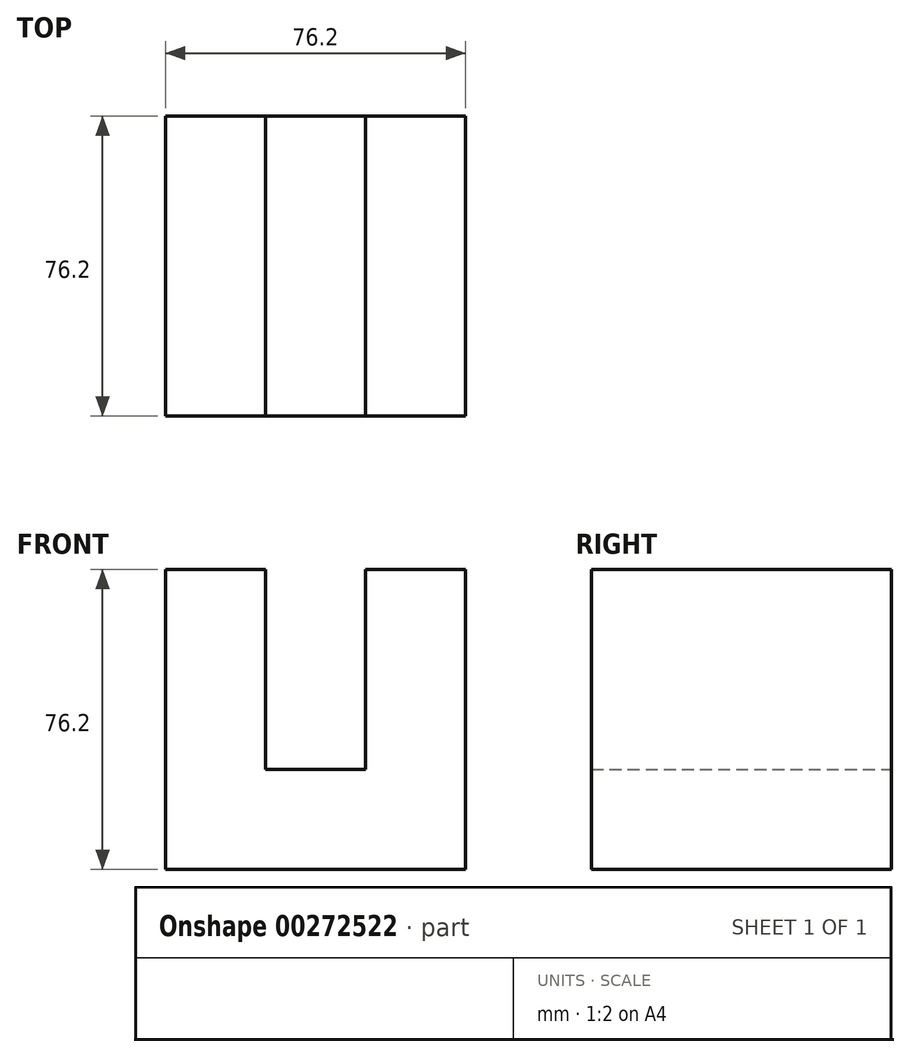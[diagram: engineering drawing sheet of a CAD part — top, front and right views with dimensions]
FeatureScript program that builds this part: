
annotation { "Feature Type Name" : "Feature", "Feature Type Description" : "" }
export const myFeature = defineFeature(function(context is Context, id is Id, definition is map)
    precondition{}
    {
        {
            var Q0;
            Q0=qCreatedBy(makeId("Front.planeOp"),FACE);
            var sketch = newSketch(context, id + "F0", { "sketchPlane" : qUnion([Q0])});
            skLineSegment(sketch, "E0", {"start": v(0, 0) * mm, "end": v(-76.2, 0) * mm});
            skLineSegment(sketch, "E1", {"start": v(-76.2, 0) * mm, "end": v(-76.2, 76.2) * mm});
            skLineSegment(sketch, "E2", {"start": v(-76.2, 76.2) * mm, "end": v(-50.8, 76.2) * mm});
            skLineSegment(sketch, "E3", {"start": v(-50.8, 76.2) * mm, "end": v(-50.8, 25.4) * mm});
            skLineSegment(sketch, "E4", {"start": v(-50.8, 25.4) * mm, "end": v(-25.4, 25.4) * mm});
            skLineSegment(sketch, "E5", {"start": v(-25.4, 25.4) * mm, "end": v(-25.4, 76.2) * mm});
            skLineSegment(sketch, "E6", {"start": v(-25.4, 76.2) * mm, "end": v(0, 76.2) * mm});
            skLineSegment(sketch, "E7", {"start": v(0, 76.2) * mm, "end": v(0, 0) * mm});
            skSolve(sketch);
        }
        {
            var Q0;
            Q0 = qSketchRegion(id + "F0", true);
            extrude(context, id + "F1", {"entities" : qUnion([Q0]), "depth" : 76.2 * mm});
        }
    });
